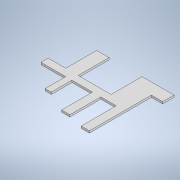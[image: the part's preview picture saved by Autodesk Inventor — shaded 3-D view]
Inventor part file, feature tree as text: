
AUTODESK INVENTOR PART (.ipt)
format: ipt  version: 2020.2 (Build 242310000, 310)  size: 130,560 bytes
history: native  units: mm
features: extrude x1, sketch x1
ambient origin geometry x8: Origin, YZ Plane, XZ Plane, XY Plane, X Axis, Y Axis, Z Axis, Center Point
bodies: Solid1 (feature_tree)
feature tree (2):
  extrude  "Extrusion1"  Depth=100.0mm
  sketch  "Sketch1"  dims[d0=5000.0mm d1=5000.0mm d2=1200.0mm d3=300.0mm d4=1000.0mm d5=2500.0mm d6=350.0mm d7=850.0mm d8=600.0mm d10=1500.0mm d12=400.0mm d13=1000.0mm d14=750.0mm d15=400.0mm d16=1700.0mm d17=400.0mm d18=3000.0mm d19=1000.0mm d20=1600.0mm d21=100.0mm d22=0.0mm]
